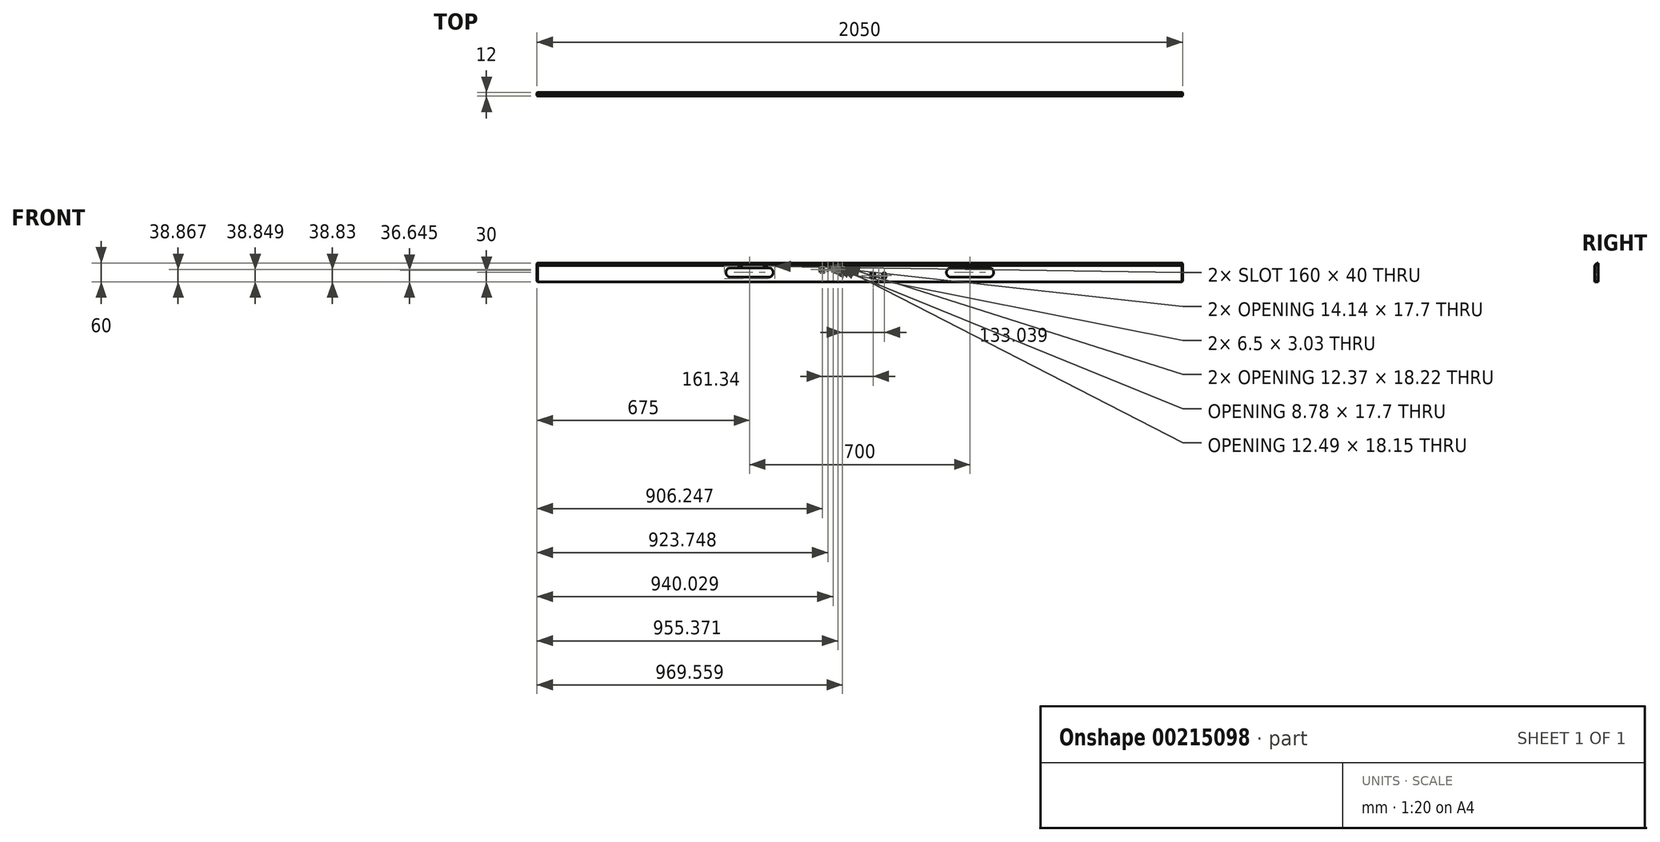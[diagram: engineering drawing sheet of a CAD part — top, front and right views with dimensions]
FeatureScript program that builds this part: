
annotation { "Feature Type Name" : "Feature", "Feature Type Description" : "" }
export const myFeature = defineFeature(function(context is Context, id is Id, definition is map)
    precondition{}
    {
        {
            var Q0;
            Q0=qCreatedBy(makeId("Front.planeOp"),FACE);
            var sketch = newSketch(context, id + "F0", { "sketchPlane" : qUnion([Q0])});
            skLineSegment(sketch, "E0.bottom", {"start": v(1025, -30) * mm, "end": v(-1025, -30) * mm});
            skLineSegment(sketch, "E0.top", {"start": v(1025, 30) * mm, "end": v(-1025, 30) * mm});
            skLineSegment(sketch, "E0.left", {"start": v(1025, -30) * mm, "end": v(1025, 30) * mm});
            skLineSegment(sketch, "E0.right", {"start": v(-1025, -30) * mm, "end": v(-1025, 30) * mm});
            skPoint(sketch, "E0.middle", {"position": v(0, 0) * mm});
            skLineSegment(sketch, "E1", {"start": v(-1025, 0) * mm, "end": v(-350, 0) * mm});
            skPoint(sketch, "E1.endSnap0", {"position": v(-1025, 0) * mm});
            skLineSegment(sketch, "E2", {"start": v(350, 0) * mm, "end": v(1025, 0) * mm});
            skPoint(sketch, "E2.startSnap0", {"position": v(1025, 0) * mm});
            skLineSegment(sketch, "E3.bottom", {"start": v(425, -15) * mm, "end": v(275, -15) * mm});
            skLineSegment(sketch, "E3.top", {"start": v(425, 15) * mm, "end": v(275, 15) * mm});
            skLineSegment(sketch, "E3.left", {"start": v(425, -15) * mm, "end": v(425, 15) * mm});
            skLineSegment(sketch, "E3.right", {"start": v(275, -15) * mm, "end": v(275, 15) * mm});
            skPoint(sketch, "E3.middle", {"position": v(350, 0) * mm});
            skLineSegment(sketch, "E4.bottom", {"start": v(-275, -15) * mm, "end": v(-425, -15) * mm});
            skLineSegment(sketch, "E4.top", {"start": v(-275, 15) * mm, "end": v(-425, 15) * mm});
            skLineSegment(sketch, "E4.left", {"start": v(-275, -15) * mm, "end": v(-275, 15) * mm});
            skLineSegment(sketch, "E4.right", {"start": v(-425, -15) * mm, "end": v(-425, 15) * mm});
            skPoint(sketch, "E4.middle", {"position": v(-350, 0) * mm});
            skText(sketch, "E5", { "text": "R - 190", "fontName": "OpenSans-Bold.ttf"});
            skText(sketch, "E6", { "text": "R - 0", "fontName": "OpenSans-Bold.ttf"});
            const initialGuessF0  = {"E5": [-0.12805, 0, 1, 0, 0.01785], "E6": [0.03329, -0.01895, 1, 0, 0.01785]};
            skSetInitialGuess(sketch, initialGuessF0);
            skSolve(sketch);
        }
        {
            var Q0;
            {var subQ1=sQuery(id+"F0.wireOp",EDGE,"E0.bottom");Q0=makeQuery(id+"F0.imprint","IMPRINT",FACE,{"disambiguationData":[TD([[makeQuery(id+"F0.imprint","IMPRINT",EDGE,{"derivedFrom":subQ1}),-1.0]])]});}
            extrude(context, id + "F1", {"entities" : qUnion([Q0]), "depth" : 12 * mm});
        }
        {
            var Q0;
            Q0=makeQuery(id+"F1.opExtrude","SWEPT_EDGE",EDGE,{"disambiguationData":[OSD([sQuery(id+"F0.wireOp",EDGE,"E4.bottom"),sQuery(id+"F0.wireOp",EDGE,"E4.left")])]});
            var Q1;
            Q1=makeQuery(id+"F1.opExtrude","SWEPT_EDGE",EDGE,{"disambiguationData":[OSD([sQuery(id+"F0.wireOp",EDGE,"E4.top"),sQuery(id+"F0.wireOp",EDGE,"E4.left")])]});
            fillet(context, id + "F2", {"entities" : qUnion([Q0, Q1]), "radius" : 15 * mm, "tangentPropagation" : true, "allowEdgeOverflow" : false});
        }
        {
            var Q0;
            Q0=makeQuery(id+"F1.opExtrude","SWEPT_EDGE",EDGE,{"disambiguationData":[OSD([sQuery(id+"F0.wireOp",EDGE,"E4.top"),sQuery(id+"F0.wireOp",EDGE,"E4.right")])]});
            var Q1;
            Q1=makeQuery(id+"F1.opExtrude","SWEPT_EDGE",EDGE,{"disambiguationData":[OSD([sQuery(id+"F0.wireOp",EDGE,"E4.bottom"),sQuery(id+"F0.wireOp",EDGE,"E4.right")])]});
            var Q2;
            Q2=makeQuery(id+"F1.opExtrude","SWEPT_EDGE",EDGE,{"disambiguationData":[OSD([sQuery(id+"F0.wireOp",EDGE,"E3.top"),sQuery(id+"F0.wireOp",EDGE,"E3.right")])]});
            var Q3;
            Q3=makeQuery(id+"F1.opExtrude","SWEPT_EDGE",EDGE,{"disambiguationData":[OSD([sQuery(id+"F0.wireOp",EDGE,"E3.bottom"),sQuery(id+"F0.wireOp",EDGE,"E3.right")])]});
            var Q4;
            Q4=makeQuery(id+"F1.opExtrude","SWEPT_EDGE",EDGE,{"disambiguationData":[OSD([sQuery(id+"F0.wireOp",EDGE,"E3.top"),sQuery(id+"F0.wireOp",EDGE,"E3.left")])]});
            var Q5;
            Q5=makeQuery(id+"F1.opExtrude","SWEPT_EDGE",EDGE,{"disambiguationData":[OSD([sQuery(id+"F0.wireOp",EDGE,"E3.bottom"),sQuery(id+"F0.wireOp",EDGE,"E3.left")])]});
            fillet(context, id + "F3", {"entities" : qUnion([Q0, Q1, Q2, Q3, Q4, Q5]), "radius" : 15 * mm, "tangentPropagation" : true, "allowEdgeOverflow" : false});
        }
        {
            var Q0;
            Q0=makeQuery(id+"F1.opExtrude","CAP_EDGE",EDGE,{"disambiguationData":[OSD([sQuery(id+"F0.wireOp",EDGE,"E0.top")])],"isStart":false});
            chamfer(context, id + "F4", {"entities" : qUnion([Q0]), "width" : 8 * mm, "tangentPropagation" : true});
        }
        {
            var Q0;
            Q0=makeQuery(id+"F1.opExtrude","CAP_EDGE",EDGE,{"disambiguationData":[OSD([sQuery(id+"F0.wireOp",EDGE,"E4.bottom")])],"isStart":false});
            var Q1;
            Q1=makeQuery(id+"F1.opExtrude","CAP_EDGE",EDGE,{"disambiguationData":[OSD([sQuery(id+"F0.wireOp",EDGE,"E4.bottom")])],"isStart":true});
            fillet(context, id + "F5", {"entities" : qUnion([Q0, Q1]), "radius" : 5 * mm, "tangentPropagation" : true, "allowEdgeOverflow" : false});
        }
        {
            var Q0;
            Q0=makeQuery(id+"F1.opExtrude","CAP_EDGE",EDGE,{"disambiguationData":[OSD([sQuery(id+"F0.wireOp",EDGE,"E3.bottom")])],"isStart":false});
            var Q1;
            Q1=makeQuery(id+"F1.opExtrude","CAP_EDGE",EDGE,{"disambiguationData":[OSD([sQuery(id+"F0.wireOp",EDGE,"E3.bottom")])],"isStart":true});
            fillet(context, id + "F6", {"entities" : qUnion([Q0, Q1]), "radius" : 5 * mm, "tangentPropagation" : true, "allowEdgeOverflow" : false});
        }
        {
            var Q0;
            Q0=makeQuery(id+"F1.opExtrude","SWEPT_EDGE",EDGE,{"disambiguationData":[OSD([sQuery(id+"F0.wireOp",EDGE,"E0.top"),sQuery(id+"F0.wireOp",EDGE,"E0.right")])]});
            var Q1;
            Q1=makeQuery(id+"F4.opChamfer","BLEND_EDGE",EDGE,{"blendedFrom":[makeQuery(id+"F1.opExtrude","CAP_EDGE",EDGE,{"disambiguationData":[OSD([sQuery(id+"F0.wireOp",EDGE,"E0.top")])],"isStart":false}),makeQuery(id+"F1.opExtrude","SWEPT_FACE",FACE,{"disambiguationData":[OSD([sQuery(id+"F0.wireOp",EDGE,"E0.right")])]})],"blendedInto":[makeQuery(id+"F1.opExtrude","SWEPT_FACE",FACE,{"disambiguationData":[OSD([sQuery(id+"F0.wireOp",EDGE,"E0.right")])]})]});
            var Q2;
            Q2=makeQuery(id+"F1.opExtrude","CAP_EDGE",EDGE,{"disambiguationData":[OSD([sQuery(id+"F0.wireOp",EDGE,"E0.right")])],"isStart":false});
            var Q3;
            Q3=makeQuery(id+"FR6XSV5B1AOtVam_1.opChamfer","BLEND_EDGE",EDGE,{"blendedFrom":[makeQuery(id+"F1.opExtrude","CAP_EDGE",EDGE,{"disambiguationData":[OSD([sQuery(id+"F0.wireOp",EDGE,"E0.bottom")])],"isStart":false}),makeQuery(id+"F1.opExtrude","SWEPT_FACE",FACE,{"disambiguationData":[OSD([sQuery(id+"F0.wireOp",EDGE,"E0.right")])]})],"blendedInto":[makeQuery(id+"F1.opExtrude","SWEPT_FACE",FACE,{"disambiguationData":[OSD([sQuery(id+"F0.wireOp",EDGE,"E0.right")])]})]});
            var Q4;
            Q4=makeQuery(id+"F1.opExtrude","SWEPT_EDGE",EDGE,{"disambiguationData":[OSD([sQuery(id+"F0.wireOp",EDGE,"E0.bottom"),sQuery(id+"F0.wireOp",EDGE,"E0.right")])]});
            var Q5;
            Q5=makeQuery(id+"F1.opExtrude","SWEPT_EDGE",EDGE,{"disambiguationData":[OSD([sQuery(id+"F0.wireOp",EDGE,"E0.top"),sQuery(id+"F0.wireOp",EDGE,"E0.left")])]});
            var Q6;
            Q6=makeQuery(id+"F4.opChamfer","BLEND_EDGE",EDGE,{"blendedFrom":[makeQuery(id+"F1.opExtrude","CAP_EDGE",EDGE,{"disambiguationData":[OSD([sQuery(id+"F0.wireOp",EDGE,"E0.top")])],"isStart":false}),makeQuery(id+"F1.opExtrude","SWEPT_FACE",FACE,{"disambiguationData":[OSD([sQuery(id+"F0.wireOp",EDGE,"E0.left")])]})],"blendedInto":[makeQuery(id+"F1.opExtrude","SWEPT_FACE",FACE,{"disambiguationData":[OSD([sQuery(id+"F0.wireOp",EDGE,"E0.left")])]})]});
            var Q7;
            Q7=makeQuery(id+"F1.opExtrude","CAP_EDGE",EDGE,{"disambiguationData":[OSD([sQuery(id+"F0.wireOp",EDGE,"E0.left")])],"isStart":false});
            var Q8;
            Q8=makeQuery(id+"FR6XSV5B1AOtVam_1.opChamfer","BLEND_EDGE",EDGE,{"blendedFrom":[makeQuery(id+"F1.opExtrude","CAP_EDGE",EDGE,{"disambiguationData":[OSD([sQuery(id+"F0.wireOp",EDGE,"E0.bottom")])],"isStart":false}),makeQuery(id+"F1.opExtrude","SWEPT_FACE",FACE,{"disambiguationData":[OSD([sQuery(id+"F0.wireOp",EDGE,"E0.left")])]})],"blendedInto":[makeQuery(id+"F1.opExtrude","SWEPT_FACE",FACE,{"disambiguationData":[OSD([sQuery(id+"F0.wireOp",EDGE,"E0.left")])]})]});
            var Q9;
            Q9=makeQuery(id+"F1.opExtrude","SWEPT_EDGE",EDGE,{"disambiguationData":[OSD([sQuery(id+"F0.wireOp",EDGE,"E0.bottom"),sQuery(id+"F0.wireOp",EDGE,"E0.left")])]});
            chamfer(context, id + "F7", {"entities" : qUnion([Q0, Q1, Q2, Q3, Q4, Q5, Q6, Q7, Q8, Q9]), "width" : 2 * mm, "tangentPropagation" : true});
        }
        {
            var Q0;
            Q0=makeQuery(id+"F1.opExtrude","CAP_EDGE",EDGE,{"disambiguationData":[OSD([sQuery(id+"F0.wireOp",EDGE,"E0.top")])],"isStart":true});
            var Q1;
            Q1=makeQuery(id+"F1.opExtrude","CAP_EDGE",EDGE,{"disambiguationData":[OSD([sQuery(id+"F0.wireOp",EDGE,"E0.left")])],"isStart":true});
            var Q2;
            Q2=makeQuery(id+"F1.opExtrude","CAP_EDGE",EDGE,{"disambiguationData":[OSD([sQuery(id+"F0.wireOp",EDGE,"E0.bottom")])],"isStart":true});
            var Q3;
            Q3=makeQuery(id+"F1.opExtrude","CAP_EDGE",EDGE,{"disambiguationData":[OSD([sQuery(id+"F0.wireOp",EDGE,"E0.right")])],"isStart":true});
            chamfer(context, id + "F8", {"entities" : qUnion([Q0, Q1, Q2, Q3]), "width" : 1 * mm, "tangentPropagation" : true});
        }
    });
